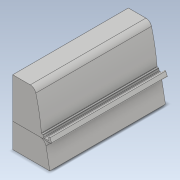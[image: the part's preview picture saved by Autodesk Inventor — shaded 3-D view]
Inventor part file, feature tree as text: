
AUTODESK INVENTOR PART (.ipt)
format: ipt  version: 2022 (Build 260153000, 153)  size: 183,808 bytes
history: native  units: mm
features: extrude x2, fillet x2, sketch x1, other x1
ambient origin geometry x8: Origin, YZ Plane, XZ Plane, XY Plane, X Axis, Y Axis, Z Axis, Center Point
bodies: Body1 (feature_tree), Body2 (feature_tree)
feature tree (6):
  extrude  "擠出1"  Depth=13.0mm
  fillet  "圓角2"  Radius=1.7mm
  extrude  "擠出2"  Depth=1.7mm
  fillet  "圓角3"  Radius=1.0mm
  sketch  "草圖4"
  other  "實體3"
